# Revit family: Deca_Torneira Mesa Decamatic Eco Conforto_ 1173.C.CONF_Fechamento Automático com Alavanca
name_source: partatom
category: Plumbing Fixtures
revit_build: Autodesk Revit Architecture 2012 (Build: 20120126_0600(x64)
units: mm (PartAtom-declared; Revit-internal decimal feet)

## types (1)
- 1173.C.CONF_Cromado CR10
    Aprovado por = Contino/quattroD
    Assembly Code = D2020
    Atendimento ao Cliente = 0800-0117073
    CWFU = 0
    Consumo = 8 L/min
    Criado por = Contino/quattroD
    Código = 1173.C.CONF
    Default Elevation = 0 mm  [stored 0 ft]
    Description = Torneira fechamento automático mesa com alavanca
    Diâmetro Água Fria = 15 mm  [stored 0.0492126 ft]
    Diâmetro Água Quente = 15 mm  [stored 0.0492126 ft]
    Flow Pressure = 0.00 psi
    HWFU = 0
    Informações Complementares = Possui restritor de  vazão constante 8 L/min.
    Linha = Decamatic Eco Conforto
    Louça/Metais = Metal
    Manufacturer = Deca
    Material = Deca_Latão Cromado e Plástico de Engenharia
    Model = 1173.C.CONF
    Monocomando = Deca CR10 Cromado Metal
    Norma = ABNT NBR 13713:2009
    Peso Liquido (Kg) = 1.339
    Pressão = 2 A 40 mca
    Produto = Torneira mesa Fechamento Automático com alavanca Decamatic Eco Conforto
    Raio Água Fria = 8 mm  [stored 0.0262467 ft]
    Raio Água Quente = 8 mm  [stored 0.0262467 ft]
    Segmento = Competitivo
    URL = www.deca.com.br/produtos
    Variações de COR = Cromado (1173.C.CONF).
    Vendido Separadamente = Ligação Flexível: 30 cm (4607.C.030), 40 cm (4607.C.040), 50 cm (4607.C.050).
    WFU = 0

note: [stored X ft] marks values corroborated as IEEE doubles in the binary element streams (Revit-internal decimal feet)

## geometry (parser evidence)
native form markers: Blend x4, Sweep x2
no freeform markers — native parametric forms only
